# Revit family: HOMECARE LIN GRAB RAIL 300 STR BAR
name_source: partatom
category: Specialty Equipment
units: mm (PartAtom-declared; Revit-internal decimal feet)

## family parameters
Cut with Voids When Loaded = No
Host = Face
OmniClass Number = 23.40.20.21.27
OmniClass Title = Towel Bars
Part Type = Normal
Room Calculation Point = No
Round Connector Dimension = Use Radius
Shared = No

## types (4) — shared parameters
Assembly Code = C1030220
Default Elevation = 1000 mm  [stored 3.28084 ft]
Manufacturer = GWA Bathrooms & Kitchens
URL = https://www.caroma.com.au

## per-type parameters (varying)
| type | Description | Material_Base | Model |
| OMECARE LIN GRAB RAIL 300 STR BAR PSS | HOMECARE LIN GRAB RAIL 300 STR BAR PSS | GWA_Metal-Polished Stainless | 98276PSS |
| HOMECARE LIN GRAB RAIL 300 STR BAR BLK | HOMECARE LIN GRAB RAIL 300 STR BAR BLK | GWA-Metal-Black | 98276B |
| HOMECARE LIN GRAB RAIL 300 STR BAR WH | HOMECARE LIN GRAB RAIL 300 STR BAR WH | GWA-Metal-White | 98276W |
| HOMECARE LIN GRAB RAIL 300 STR BAR BN | HOMECARE LIN GRAB RAIL 300 STR BAR BN | GWA_Metal-Brushed-Nickel | 98276BN |

note: [stored X ft] marks values corroborated as IEEE doubles in the binary element streams (Revit-internal decimal feet)

## geometry (parser evidence)
native form markers: Sweep x2
no freeform markers — native parametric forms only
